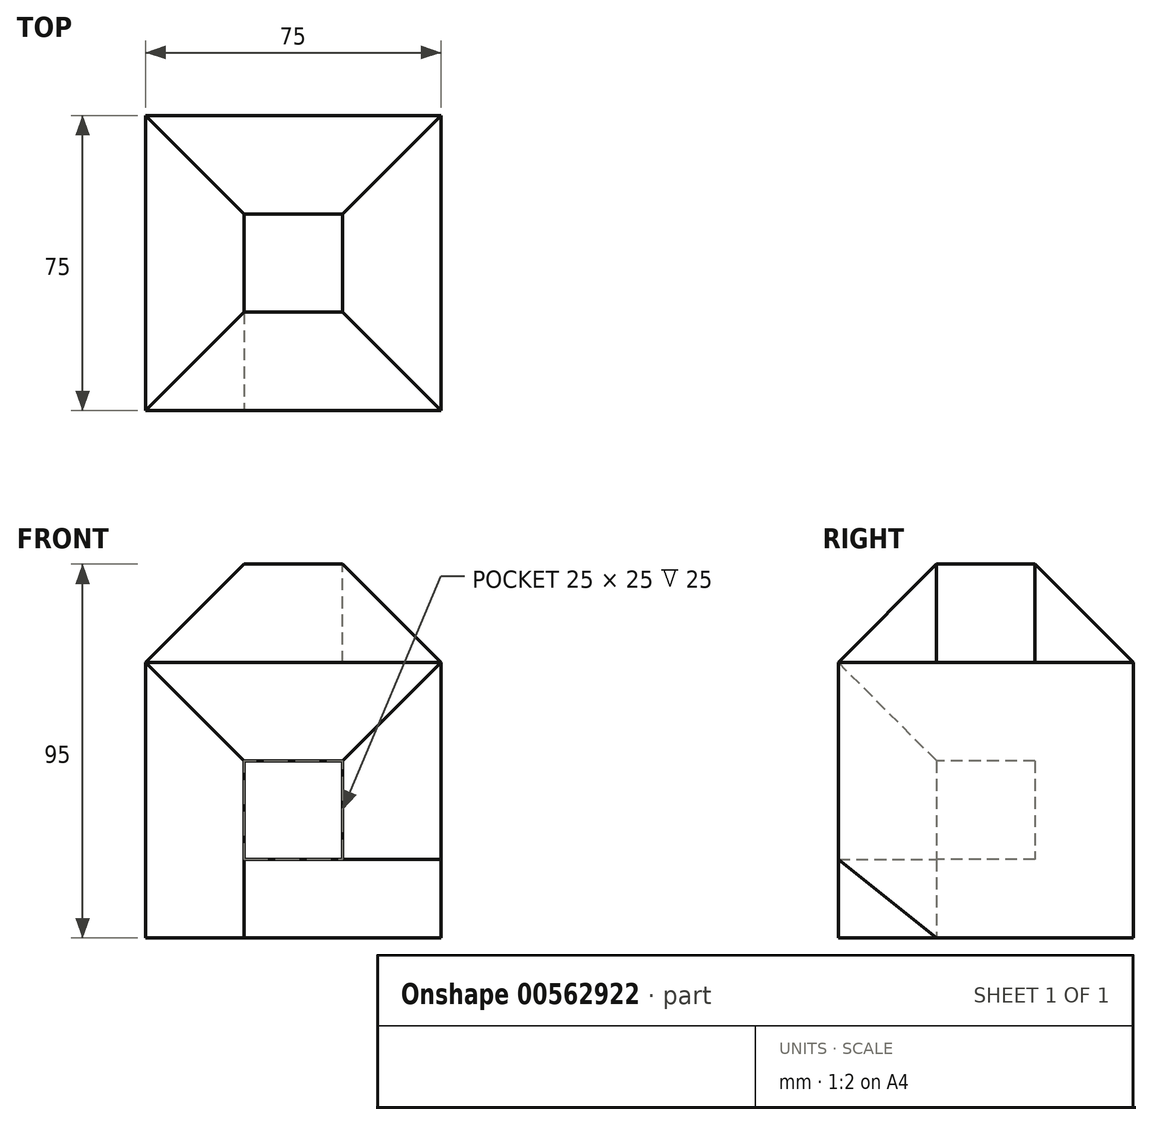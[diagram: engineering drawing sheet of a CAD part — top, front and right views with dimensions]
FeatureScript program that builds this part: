
annotation { "Feature Type Name" : "Feature", "Feature Type Description" : "" }
export const myFeature = defineFeature(function(context is Context, id is Id, definition is map)
    precondition{}
    {
        {
            var Q0;
            Q0=qCreatedBy(makeId("Top.planeOp"),FACE);
            cPlane(context, id + "F0", {"entities" : qUnion([Q0]), "cplaneType" : CPlaneType.OFFSET, "offset" : 20 * mm, "width" : 150 * mm, "height" : 150 * mm});
        }
        {
            var Q0;
            Q0=qCreatedBy(id+"F0.planeOp",FACE);
            cPlane(context, id + "F1", {"entities" : qUnion([Q0]), "cplaneType" : CPlaneType.OFFSET, "offset" : 25 * mm, "width" : 150 * mm, "height" : 150 * mm});
        }
        {
            var Q0;
            Q0=qCreatedBy(id+"F1.planeOp",FACE);
            cPlane(context, id + "F2", {"entities" : qUnion([Q0]), "cplaneType" : CPlaneType.OFFSET, "offset" : 25 * mm, "width" : 150 * mm, "height" : 150 * mm});
        }
        {
            var Q0;
            Q0=qCreatedBy(id+"F2.planeOp",FACE);
            cPlane(context, id + "F3", {"entities" : qUnion([Q0]), "cplaneType" : CPlaneType.OFFSET, "offset" : 25 * mm, "width" : 150 * mm, "height" : 150 * mm});
        }
        {
            var Q0;
            Q0=qCreatedBy(id+"F3.planeOp",FACE);
            var sketch = newSketch(context, id + "F4", { "sketchPlane" : qUnion([Q0])});
            skLineSegment(sketch, "E0.bottom", {"start": v(12.5, 12.5) * mm, "end": v(-12.5, 12.5) * mm});
            skLineSegment(sketch, "E0.top", {"start": v(12.5, -12.5) * mm, "end": v(-12.5, -12.5) * mm});
            skLineSegment(sketch, "E0.left", {"start": v(12.5, 12.5) * mm, "end": v(12.5, -12.5) * mm});
            skLineSegment(sketch, "E0.right", {"start": v(-12.5, 12.5) * mm, "end": v(-12.5, -12.5) * mm});
            skPoint(sketch, "E0.middle", {"position": v(0, 0) * mm});
            skSolve(sketch);
        }
        {
            var Q0;
            Q0=qCreatedBy(id+"F2.planeOp",FACE);
            var sketch = newSketch(context, id + "F5", { "sketchPlane" : qUnion([Q0])});
            skLineSegment(sketch, "E1.bottom", {"start": v(37.5, -37.5) * mm, "end": v(-37.5, -37.5) * mm});
            skLineSegment(sketch, "E1.top", {"start": v(37.5, 37.5) * mm, "end": v(-37.5, 37.5) * mm});
            skLineSegment(sketch, "E1.left", {"start": v(37.5, -37.5) * mm, "end": v(37.5, 37.5) * mm});
            skLineSegment(sketch, "E1.right", {"start": v(-37.5, -37.5) * mm, "end": v(-37.5, 37.5) * mm});
            skPoint(sketch, "E1.middle", {"position": v(0, 0) * mm});
            skSolve(sketch);
        }
        {
            var Q0;
            Q0=makeQuery(id+"F5.imprint","IMPRINT",FACE,{"disambiguationData":[TD([[makeQuery(id+"F5.imprint","IMPRINT",EDGE,{"derivedFrom":sQuery(id+"F5.wireOp",EDGE,"E1.bottom")}),-1.0]])]});
            var Q1;
            Q1=makeQuery(id+"F4.imprint","IMPRINT",FACE,{"disambiguationData":[TD([[makeQuery(id+"F4.imprint","IMPRINT",EDGE,{"derivedFrom":sQuery(id+"F4.wireOp",EDGE,"E0.bottom")}),1.0]])]});
            loft(context, id + "F6", {"sheetProfilesArray" : [{ "sheetProfileEntities" : qUnion([Q0]) }, { "sheetProfileEntities" : qUnion([Q1]) }]});
        }
        {
            var Q0;
            Q0=qCreatedBy(id+"F1.planeOp",FACE);
            var sketch = newSketch(context, id + "F7", { "sketchPlane" : qUnion([Q0])});
            skLineSegment(sketch, "E2.bottom", {"start": v(12.5, 12.5) * mm, "end": v(-12.5, 12.5) * mm});
            skLineSegment(sketch, "E2.top", {"start": v(12.5, -12.5) * mm, "end": v(-12.5, -12.5) * mm});
            skLineSegment(sketch, "E2.left", {"start": v(12.5, 12.5) * mm, "end": v(12.5, -12.5) * mm});
            skLineSegment(sketch, "E2.right", {"start": v(-12.5, 12.5) * mm, "end": v(-12.5, -12.5) * mm});
            skPoint(sketch, "E2.middle", {"position": v(0, 0) * mm});
            skSolve(sketch);
        }
        {
            var Q1;
            Q1 = qSketchRegion(id + "F5", true);
            var Q2;
            Q2 = qSketchRegion(id + "F7", true);
            loft(context, id + "F8", {"operationType" : NewBodyOperationType.ADD, "sheetProfilesArray" : [{ "sheetProfileEntities" : qUnion([Q1]) }, { "sheetProfileEntities" : qUnion([Q2]) }]});
        }
        {
            var Q0;
            Q0=qCreatedBy(makeId("Top.planeOp"),FACE);
            var sketch = newSketch(context, id + "F9", { "sketchPlane" : qUnion([Q0])});
            skLineSegment(sketch, "E3.0", {"start": v(-37.5, -37.5) * mm, "end": v(37.5, -37.5) * mm});
            skLineSegment(sketch, "E4.0", {"start": v(37.5, -37.5) * mm, "end": v(37.5, 37.5) * mm});
            skLineSegment(sketch, "E5.0", {"start": v(37.5, 37.5) * mm, "end": v(-37.5, 37.5) * mm});
            skLineSegment(sketch, "E6.0", {"start": v(-37.5, 37.5) * mm, "end": v(-37.5, -37.5) * mm});
            skLineSegment(sketch, "E7.0", {"start": v(37.5, -37.5) * mm, "end": v(12.5, -12.5) * mm});
            skLineSegment(sketch, "E8.0", {"start": v(-37.5, -37.5) * mm, "end": v(-12.5, -12.5) * mm});
            skLineSegment(sketch, "E9.0", {"start": v(37.5, 37.5) * mm, "end": v(12.5, 12.5) * mm});
            skLineSegment(sketch, "E10.0", {"start": v(-37.5, 37.5) * mm, "end": v(-12.5, 12.5) * mm});
            skLineSegment(sketch, "E11.0.0", {"start": v(12.5, -12.5) * mm, "end": v(-12.5, -12.5) * mm});
            skLineSegment(sketch, "E11.0.1", {"start": v(-12.5, -12.5) * mm, "end": v(-12.5, 12.5) * mm});
            skLineSegment(sketch, "E11.0.2", {"start": v(-12.5, 12.5) * mm, "end": v(12.5, 12.5) * mm});
            skLineSegment(sketch, "E11.0.3", {"start": v(12.5, 12.5) * mm, "end": v(12.5, -12.5) * mm});
            skSolve(sketch);
        }
        {
            var Q0;
            Q0=makeQuery(id+"F9.imprint","IMPRINT",FACE,{"disambiguationData":[TD([[makeQuery(id+"F9.imprint","IMPRINT",EDGE,{"derivedFrom":sQuery(id+"F9.wireOp",EDGE,"E5.0")}),1.0]])]});
            extrude(context, id + "F10", {"entities" : qUnion([Q0]), "operationType" : NewBodyOperationType.ADD, "endBound" : BoundingType.UP_TO_NEXT, "depth" : 25 * mm, "offsetDistance" : 25 * mm});
        }
        {
            var Q0;
            Q0=makeQuery(id+"F9.imprint","IMPRINT",FACE,{"disambiguationData":[TD([[makeQuery(id+"F9.imprint","IMPRINT",EDGE,{"derivedFrom":sQuery(id+"F9.wireOp",EDGE,"E6.0")}),1.0]])]});
            extrude(context, id + "F11", {"entities" : qUnion([Q0]), "operationType" : NewBodyOperationType.ADD, "endBound" : BoundingType.UP_TO_NEXT, "depth" : 25 * mm, "offsetDistance" : 25 * mm});
        }
        {
            var Q0;
            Q0=makeQuery(id+"F9.imprint","IMPRINT",FACE,{"disambiguationData":[TD([[makeQuery(id+"F9.imprint","IMPRINT",EDGE,{"derivedFrom":sQuery(id+"F9.wireOp",EDGE,"E4.0")}),1.0]])]});
            extrude(context, id + "F12", {"entities" : qUnion([Q0]), "operationType" : NewBodyOperationType.ADD, "endBound" : BoundingType.UP_TO_NEXT, "depth" : 25 * mm, "offsetDistance" : 25 * mm});
        }
        {
            var Q0;
            Q0=qCreatedBy(makeId("Right.planeOp"),FACE);
            var sketch = newSketch(context, id + "F13", { "sketchPlane" : qUnion([Q0])});
            skLineSegment(sketch, "E12", {"start": v(-12.5, 0) * mm, "end": v(-37.5, 20) * mm});
            skLineSegment(sketch, "E13", {"start": v(-37.5, 20) * mm, "end": v(12.5, 20) * mm});
            skLineSegment(sketch, "E14", {"start": v(12.5, 20) * mm, "end": v(12.5, 0) * mm});
            skLineSegment(sketch, "E15", {"start": v(12.5, 0) * mm, "end": v(-12.5, 0) * mm});
            skSolve(sketch);
        }
        {
            var Q0;
            Q0 = qSketchRegion(id + "F13", true);
            var Q1;
            Q1=makeQuery(id+"F12.opExtrude","SWEPT_FACE",FACE,{"disambiguationData":[OSD([sQuery(id+"F9.wireOp",EDGE,"E4.0")])]});
            var Q2;
            Q2=makeQuery(id+"F11.opExtrude","SWEPT_FACE",FACE,{"disambiguationData":[OSD([sQuery(id+"F9.wireOp",EDGE,"E11.0.1")])]});
            extrude(context, id + "F14", {"entities" : qUnion([Q0]), "operationType" : NewBodyOperationType.ADD, "endBound" : BoundingType.UP_TO_SURFACE, "depth" : 25 * mm, "endBoundEntityFace" : qUnion([Q1]), "offsetDistance" : 25 * mm, "hasSecondDirection" : true, "secondDirectionBound" : SecondDirectionBoundingType.UP_TO_SURFACE, "secondDirectionOppositeDirection" : true, "secondDirectionDepth" : 25 * mm, "secondDirectionBoundEntityFace" : qUnion([Q2])});
        }
        {
            var Q0;
            Q0=makeQuery(id+"F12.opExtrude","SWEPT_FACE",FACE,{"disambiguationData":[OSD([sQuery(id+"F9.wireOp",EDGE,"E4.0")])]});
            var sketch = newSketch(context, id + "F15", { "sketchPlane" : qUnion([Q0])});
            skLineSegment(sketch, "E16.0", {"start": v(-12.5, 0) * mm, "end": v(-37.5, 20) * mm});
            skLineSegment(sketch, "E17.0", {"start": v(-37.5, 20) * mm, "end": v(-37.5, 0) * mm});
            skLineSegment(sketch, "E18.0", {"start": v(-37.5, 0) * mm, "end": v(-12.5, 0) * mm});
            skPoint(sketch, "E19.orphan", {"position": v(37.5, 0) * mm});
            skSolve(sketch);
        }
        {
            var Q0;
            Q0 = qSketchRegion(id + "F15", true);
            var Q1;
            Q1=makeQuery(id+"F11.opExtrude","SWEPT_FACE",FACE,{"disambiguationData":[OSD([sQuery(id+"F9.wireOp",EDGE,"E8.0")])]});
            extrude(context, id + "F16", {"entities" : qUnion([Q0]), "operationType" : NewBodyOperationType.REMOVE, "endBound" : BoundingType.UP_TO_SURFACE, "oppositeDirection" : true, "depth" : 25 * mm, "endBoundEntityFace" : qUnion([Q1]), "offsetDistance" : 25 * mm});
        }
        {
            var Q0;
            Q0=qCreatedBy(id+"F3.planeOp",FACE);
            var sketch = newSketch(context, id + "F17", { "sketchPlane" : qUnion([Q0])});
            skLineSegment(sketch, "E20.0", {"start": v(12.5, -12.5) * mm, "end": v(12.5, 12.5) * mm});
            skLineSegment(sketch, "E21.0.0", {"start": v(37.5, 37.5) * mm, "end": v(12.5, 12.5) * mm});
            skLineSegment(sketch, "E21.0.3", {"start": v(37.5, -12.5) * mm, "end": v(37.5, 37.5) * mm});
            skPoint(sketch, "E21.0.2.end.orphan", {"position": v(37.5, -37.5) * mm});
            skLineSegment(sketch, "E22.0.2", {"start": v(12.5, -12.5) * mm, "end": v(37.5, -37.5) * mm});
            skLineSegment(sketch, "E22.0.3", {"start": v(37.5, -37.5) * mm, "end": v(37.5, 37.5) * mm});
            skSolve(sketch);
        }
        {
            var Q0;
            Q0 = qSketchRegion(id + "F17", true);
            var Q1;
            Q1=qCreatedBy(id+"F2.planeOp",FACE);
            extrude(context, id + "F18", {"entities" : qUnion([Q0]), "operationType" : NewBodyOperationType.REMOVE, "endBound" : BoundingType.UP_TO_SURFACE, "oppositeDirection" : true, "depth" : 25 * mm, "endBoundEntityFace" : qUnion([Q1]), "offsetDistance" : 25 * mm});
        }
    });
